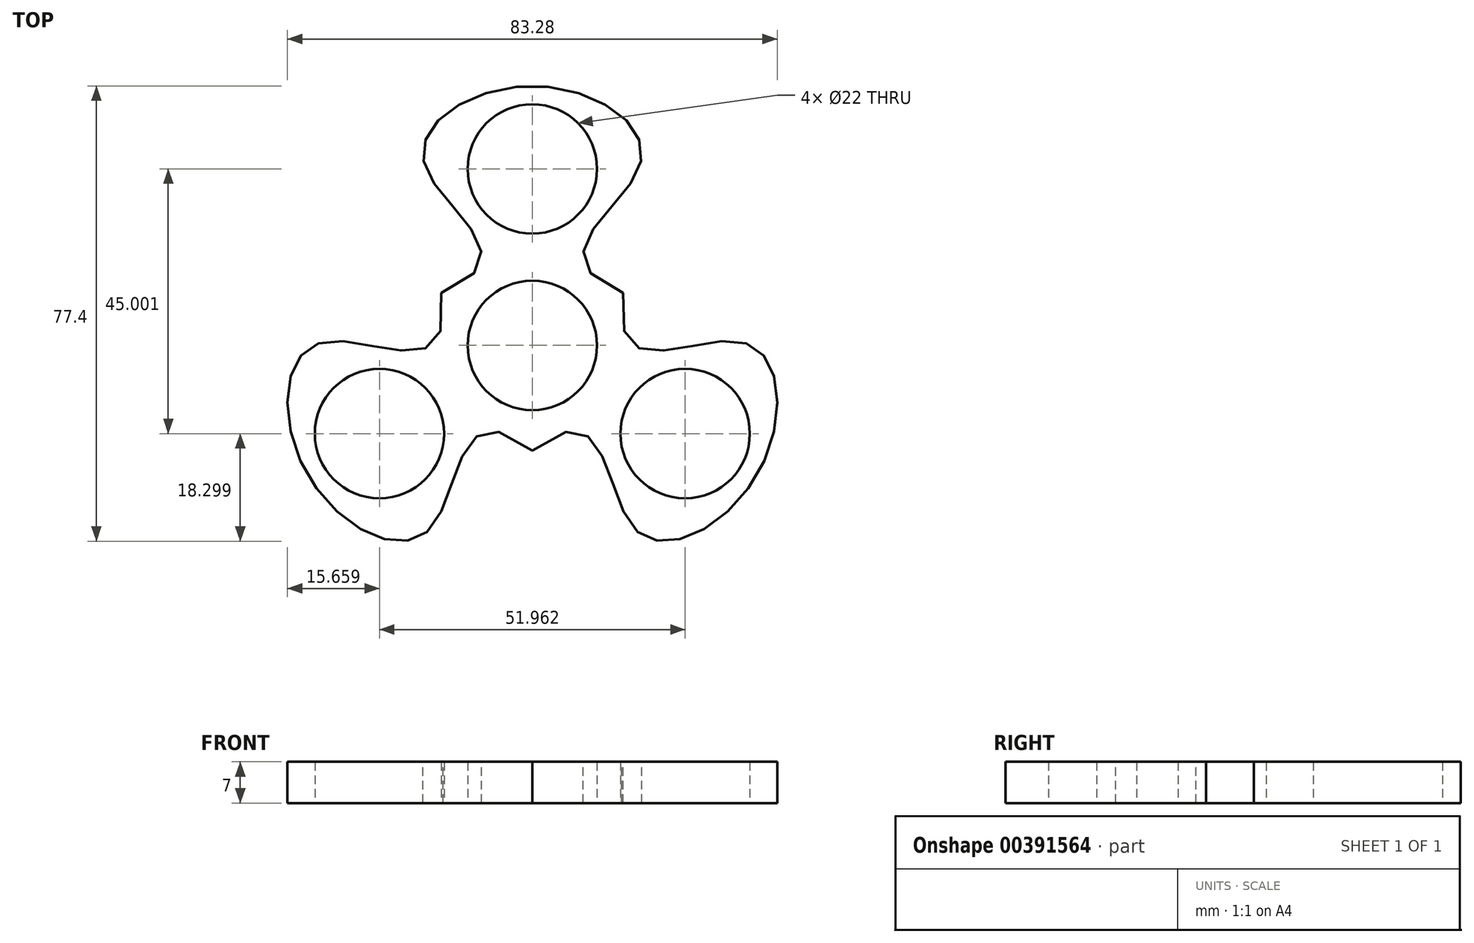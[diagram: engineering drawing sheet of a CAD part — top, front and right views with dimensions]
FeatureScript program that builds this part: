
annotation { "Feature Type Name" : "Feature", "Feature Type Description" : "" }
export const myFeature = defineFeature(function(context is Context, id is Id, definition is map)
    precondition{}
    {
        {
            var Q0;
            Q0=qCreatedBy(makeId("Top.planeOp"),FACE);
            var sketch = newSketch(context, id + "F0", { "sketchPlane" : qUnion([Q0])});
            skCircle(sketch, "E0", {"center": v(0, 0) * mm, "radius": 11 * mm});
            skCircle(sketch, "E1", {"center": v(0, 30) * mm, "radius": 11 * mm});
            skLineSegment(sketch, "E2", {"start": v(0, 30) * mm, "end": v(0, 0) * mm, "construction": true});
            skFitSpline(sketch, "E3", {"points": [v(0, -17.85) * mm, v(-16.93, -30.68) * mm, v(-38.2, -22.05) * mm, v(-35.03, 0.67) * mm, v(-15.46, 8.93) * mm], "startDerivative": vector(-158.96, 126.7) * mm, "endDerivative": vector(-30.24, 201) * mm});
            skCircle(sketch, "E4.1.2", {"center": v(-25.98, -15) * mm, "radius": 11 * mm});
            skCircle(sketch, "E4.2.2", {"center": v(25.98, -15) * mm, "radius": 11 * mm});
            skFitSpline(sketch, "E5", {"points": [v(15.46, 8.93) * mm, v(35.03, 0.67) * mm, v(38.2, -22.05) * mm, v(16.93, -30.68) * mm, v(0, -17.85) * mm], "startDerivative": vector(-30.24, -201) * mm, "endDerivative": vector(-158.63, -127.15) * mm});
            skFitSpline(sketch, "E6", {"points": [v(-15.46, 8.93) * mm, v(-18.1, 30) * mm, v(0, 44.1) * mm, v(18.1, 30) * mm, v(15.46, 8.93) * mm], "startDerivative": vector(189.2, 74.32) * mm, "endDerivative": vector(189.2, -74.32) * mm});
            skSolve(sketch);
        }
        {
            var Q0;
            Q0=makeQuery(id+"F0.imprint","IMPRINT",FACE,{"disambiguationData":[TD([[makeQuery(id+"F0.imprint","IMPRINT",EDGE,{"derivedFrom":sQuery(id+"F0.wireOp",EDGE,"E0")}),-1.0]])]});
            extrude(context, id + "F1", {"entities" : qUnion([Q0]), "endBound" : BoundingType.SYMMETRIC, "depth" : 7 * mm});
        }
    });
